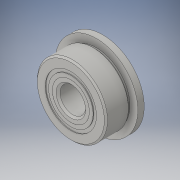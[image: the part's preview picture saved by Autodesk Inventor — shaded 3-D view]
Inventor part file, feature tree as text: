
AUTODESK INVENTOR PART (.ipt)
format: ipt  version: 2016 (Build 200138000, 138)  size: 578,048 bytes
history: native  units: in
note: dims shown in document units (in); Inventor stores cm internally (conversion verified against a paired STEP export)
features: other x10, revolve x5
ambient origin geometry x8: Origin, YZ Plane, XZ Plane, XY Plane, X Axis, Y Axis, Z Axis, Center Point
bodies: Solid1 (feature_tree), Solid2 (feature_tree), Solid3 (feature_tree), Solid4 (feature_tree), Solid5 (feature_tree), Solid6 (feature_tree), Solid7 (feature_tree), Solid8 (feature_tree), Solid9 (feature_tree), Solid10 (feature_tree), Solid11 (feature_tree), Solid12 (feature_tree), Solid13 (feature_tree), Solid14 (feature_tree), Solid15 (feature_tree)
feature tree (15):
  revolve  "Revolve2"  [1 undecoded]
  revolve  "Revolve3"  [1 undecoded]
  other  "Cut-Revolve1"
  revolve  "Revolve4"  [1 undecoded]
  other  "CirPattern1[1]"
  other  "CirPattern1[2]"
  other  "CirPattern1[3]"
  other  "CirPattern1[4]"
  other  "CirPattern1[5]"
  other  "CirPattern1[6]"
  other  "CirPattern1[7]"
  other  "CirPattern1[8]"
  other  "CirPattern1[9]"
  revolve  "Revolve6[1]"  [1 undecoded]
  revolve  "Revolve6[2]"  [1 undecoded]
note: 5 required parameter values undecoded (feature->parameter linkage not recoverable at this tier; creation-order binding heuristic only, values carry confidence <= 0.55)
